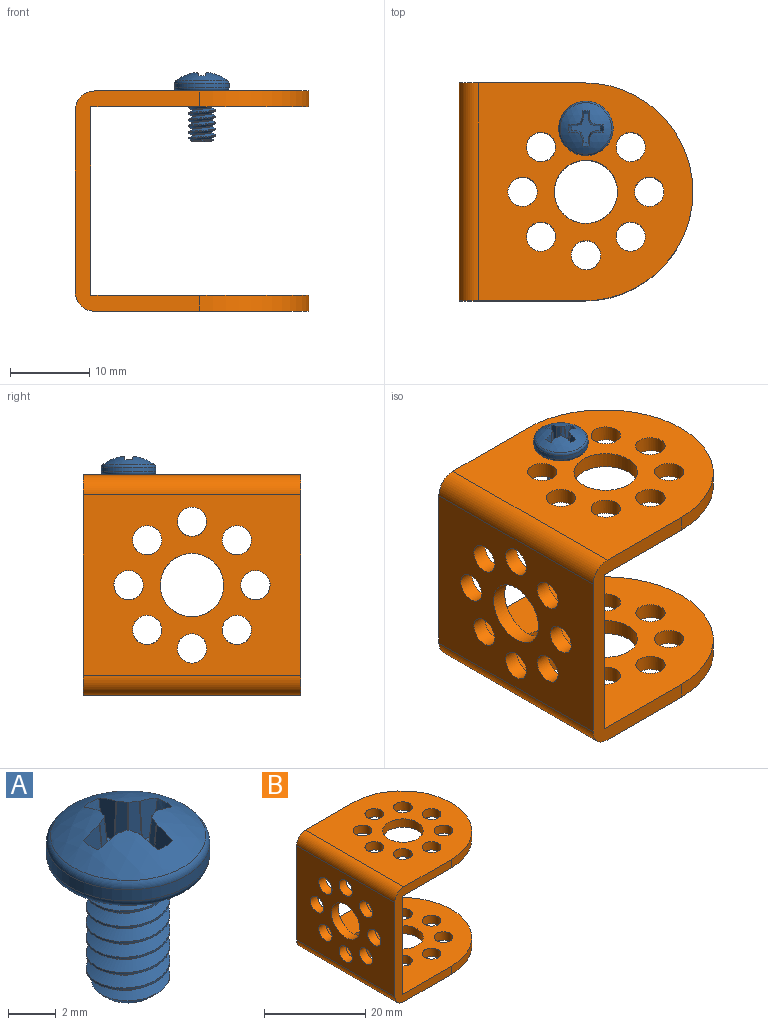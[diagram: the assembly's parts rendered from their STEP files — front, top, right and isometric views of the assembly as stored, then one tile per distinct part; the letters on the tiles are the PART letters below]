
ASSEMBLY  parts=2 mates=1
PART A: 45 faces, bbox 7.7x7.7x9.2 mm
  f0: cone r=2.38mm half-angle=15deg, axis (0,0,1), area 1.3mm2, adj f3,f19,f23,f24
  f1: cone r=2.38mm half-angle=15deg, axis (0,0,1), area 1.3mm2, adj f3,f18,f19,f20
  f2: torus R=2.99mm, axis (0,0,1), area 8.7mm2, adj f3,f4
  f3: sphere r=5.39mm, area 28.4mm2, adj f0,f1,f2,f14,f15,f16,f17,f18
  f4: cylinder r=3.43mm len=6.86mm, axis (0,0,-1), area 12.4mm2, adj f2,f5
  f5: torus R=2.99mm, axis (0,0,1), area 14.3mm2, adj f4,f9
  f6: cone r=4.41mm half-angle=45deg, axis (0,0,1), area 3.3mm2, adj f8,f10,f11,f12,f13
  f7: cylinder r=1.24mm len=6.35mm, axis (0,0,1), area 6.2mm2, adj f9,f10,f11,f12,f13
  f8: cylinder r=1.75mm len=5.83mm, axis (0,0,1), area 8mm2, adj f6,f9,f10,f11
  f9: plane 6.28x6.28mm, normal (0,0,-1), area 20.9mm2, adj f5,f7,f8,f10,f11
  f10: bspline ~6.6x3.5mm, area 42.5mm2, adj f6,f7,f8,f9,f12
  f11: bspline ~6.65x3.5mm, area 42.9mm2, adj f6,f7,f8,f9
  f12: bspline ~2.8x1.46mm, area 0.5mm2, adj f6,f7,f10
  f13: plane 2.47x2.47mm, normal (0,0,-1), area 4.8mm2, adj f6,f7
  f14: cone r=2.38mm half-angle=15deg, axis (0,0,1), area 1.3mm2, adj f3,f15,f19,f32
  f15: plane 1.94x1.03mm, normal (-1,0,0.09), area 1.5mm2, adj f3,f14,f19,f38
  f16: plane 2x0.56mm, normal (-0.92,-0.38,0.09), area 1mm2, adj f3,f19,f37,f38
  f17: plane 2x0.56mm, normal (-0.38,-0.92,0.09), area 1mm2, adj f3,f19,f36,f37
  f18: plane 1.94x1.03mm, normal (0,-1,0.09), area 1.5mm2, adj f1,f3,f19,f36
  f19: plane 3.64x3.64mm, normal (0,0,1), area 5.1mm2, adj f0,f1,f14,f15,f16,f17,f18,f20
  f20: plane 1.94x1.03mm, normal (0,1,0.09), area 1.5mm2, adj f1,f3,f19,f40
  f21: plane 2x0.56mm, normal (-0.38,0.92,0.09), area 1mm2, adj f3,f19,f40,f41
  f22: plane 2x0.56mm, normal (-0.92,0.38,0.09), area 1mm2, adj f3,f19,f39,f41
  f23: plane 1.94x1.03mm, normal (-1,0,0.09), area 1.5mm2, adj f0,f3,f19,f39
  f24: plane 1.94x1.03mm, normal (1,0,0.09), area 1.5mm2, adj f0,f3,f19,f42
  f25: plane 2x0.56mm, normal (0.92,0.38,0.09), area 1mm2, adj f3,f19,f42,f44
  f26: plane 2x0.56mm, normal (0.38,0.92,0.09), area 1mm2, adj f3,f19,f43,f44
  f27: plane 1.94x1.03mm, normal (0,1,0.09), area 1.5mm2, adj f3,f19,f28,f43
  f28: cone r=2.38mm half-angle=15deg, axis (0,0,1), area 1.3mm2, adj f3,f19,f27,f29
  f29: plane 1.94x1.03mm, normal (0,-1,0.09), area 1.5mm2, adj f3,f19,f28,f33
  f30: plane 2x0.56mm, normal (0.38,-0.92,0.09), area 1mm2, adj f3,f19,f33,f34
  f31: plane 2x0.56mm, normal (0.92,-0.38,0.09), area 1mm2, adj f3,f19,f34,f35
  f32: plane 1.94x1.03mm, normal (1,0,0.09), area 1.5mm2, adj f3,f14,f19,f35
  f33: cylinder r=0.1mm len=1.94mm, axis (-0.02,0.09,1), area 0.1mm2, adj f3,f19,f29,f30
  f34: cylinder r=0.1mm len=2mm, axis (-0.07,0.07,1), area 0.2mm2, adj f3,f19,f30,f31
  f35: cylinder r=0.1mm len=1.94mm, axis (-0.09,0.02,1), area 0.1mm2, adj f3,f19,f31,f32
  f36: cylinder r=0.1mm len=1.94mm, axis (0.02,0.09,1), area 0.1mm2, adj f3,f17,f18,f19
  f37: cylinder r=0.1mm len=2mm, axis (0.07,0.07,1), area 0.2mm2, adj f3,f16,f17,f19
  f38: cylinder r=0.1mm len=1.94mm, axis (0.09,0.02,1), area 0.1mm2, adj f3,f15,f16,f19
  f39: cylinder r=0.1mm len=1.94mm, axis (0.09,-0.02,1), area 0.1mm2, adj f3,f19,f22,f23
  f40: cylinder r=0.1mm len=1.94mm, axis (0.02,-0.09,1), area 0.1mm2, adj f3,f19,f20,f21
  f41: cylinder r=0.1mm len=2mm, axis (0.07,-0.07,1), area 0.2mm2, adj f3,f19,f21,f22
  f42: cylinder r=0.1mm len=1.94mm, axis (-0.09,-0.02,1), area 0.1mm2, adj f3,f19,f24,f25
  f43: cylinder r=0.1mm len=1.94mm, axis (-0.02,-0.09,1), area 0.1mm2, adj f3,f19,f26,f27
  f44: cylinder r=0.1mm len=2mm, axis (-0.07,-0.07,1), area 0.2mm2, adj f3,f19,f25,f26
PART B: 39 faces, bbox 29.5x27.5x27.8 mm
  f0: cylinder r=1.85mm len=3.7mm, axis (-1,0,0), area 23.2mm2, adj f27,f32
  f1: cylinder r=1.85mm len=3.7mm, axis (-1,0,0), area 23.2mm2, adj f27,f32
  f2: cylinder r=1.85mm len=3.7mm, axis (-1,0,0), area 23.2mm2, adj f27,f32
  f3: cylinder r=1.85mm len=3.7mm, axis (-1,0,0), area 23.2mm2, adj f27,f32
  f4: cylinder r=1.85mm len=3.7mm, axis (-1,0,0), area 23.2mm2, adj f27,f32
  f5: cylinder r=1.85mm len=3.7mm, axis (-1,0,0), area 23.2mm2, adj f27,f32
  f6: cylinder r=1.85mm len=3.7mm, axis (-1,0,0), area 23.2mm2, adj f27,f32
  f7: cylinder r=1.85mm len=3.7mm, axis (-1,0,0), area 23.2mm2, adj f27,f32
  f8: cylinder r=4mm len=8mm, axis (-1,0,0), area 50.3mm2, adj f27,f32
  f9: cylinder r=1.85mm len=3.7mm, axis (0,0,1), area 23.2mm2, adj f30,f33
  f10: cylinder r=1.85mm len=3.7mm, axis (0,0,1), area 23.2mm2, adj f28,f34
  f11: cylinder r=1.85mm len=3.7mm, axis (0,0,1), area 23.2mm2, adj f30,f33
  f12: cylinder r=1.85mm len=3.7mm, axis (0,0,1), area 23.2mm2, adj f28,f34
  f13: cylinder r=1.85mm len=3.7mm, axis (0,0,1), area 23.2mm2, adj f30,f33
  f14: cylinder r=1.85mm len=3.7mm, axis (0,0,1), area 23.2mm2, adj f28,f34
  f15: cylinder r=1.85mm len=3.7mm, axis (0,0,1), area 23.2mm2, adj f30,f33
  f16: cylinder r=1.85mm len=3.7mm, axis (0,0,1), area 23.2mm2, adj f28,f34
  f17: cylinder r=1.85mm len=3.7mm, axis (0,0,1), area 23.2mm2, adj f30,f33
  f18: cylinder r=1.85mm len=3.7mm, axis (0,0,1), area 23.2mm2, adj f28,f34
  f19: cylinder r=1.85mm len=3.7mm, axis (0,0,1), area 23.2mm2, adj f30,f33
  f20: cylinder r=1.85mm len=3.7mm, axis (0,0,1), area 23.2mm2, adj f28,f34
  f21: cylinder r=1.85mm len=3.7mm, axis (0,0,1), area 23.2mm2, adj f30,f33
  f22: cylinder r=1.85mm len=3.7mm, axis (0,0,1), area 23.2mm2, adj f28,f34
  f23: cylinder r=1.85mm len=3.7mm, axis (0,0,1), area 23.2mm2, adj f30,f33
  f24: cylinder r=1.85mm len=3.7mm, axis (0,0,1), area 23.2mm2, adj f28,f34
  f25: cylinder r=4mm len=8mm, axis (0,0,1), area 50.3mm2, adj f30,f33
  f26: cylinder r=4mm len=8mm, axis (0,0,1), area 50.3mm2, adj f28,f34
  f27: plane 27.5x23.8mm, normal (1,0,0), area 518.2mm2, adj f0,f1,f2,f3,f4,f5,f6,f7
  f28: plane 27.5x27mm, normal (0,0,-1), area 525.1mm2, adj f10,f12,f14,f16,f18,f20,f22,f24
  f29: plane 27.8x15.75mm, normal (0,1,0), area 107.9mm2, adj f27,f28,f30,f32,f33,f34,f35,f36
  f30: plane 27.5x27mm, normal (0,0,1), area 525.1mm2, adj f9,f11,f13,f15,f17,f19,f21,f23
  f31: plane 27.8x15.75mm, normal (0,-1,0), area 107.9mm2, adj f27,f28,f30,f32,f33,f34,f35,f36
  f32: plane 27.5x22.8mm, normal (-1,0,0), area 490.7mm2, adj f0,f1,f2,f3,f4,f5,f6,f7
  f33: plane 27.5x27.5mm, normal (0,0,-1), area 538.8mm2, adj f9,f11,f13,f15,f17,f19,f21,f23
  f34: plane 27.5x27.5mm, normal (0,0,1), area 538.8mm2, adj f10,f12,f14,f16,f18,f20,f22,f24
  f35: cylinder r=13.75mm len=27.5mm, axis (0,0,1), area 86.4mm2, adj f28,f29,f31,f34
  f36: cylinder r=13.75mm len=27.5mm, axis (0,0,-1), area 86.4mm2, adj f29,f30,f31,f33
  f37: cylinder r=2.5mm len=27.5mm, axis (0,-1,0), area 108mm2, adj f29,f30,f31,f32
  f38: cylinder r=2.5mm len=27.5mm, axis (0,1,0), area 108mm2, adj f28,f29,f31,f32
PLACE A rot(axis=(0,0,-1),90deg) t=(20.17,0.21,7.51)mm
PLACE B t=(4.17,-7.79,0.03)mm fixed
MATE fastened B.f17 <-> A.f5  axis (0,0,-1) through (20.17,0.21,11.93)mm
